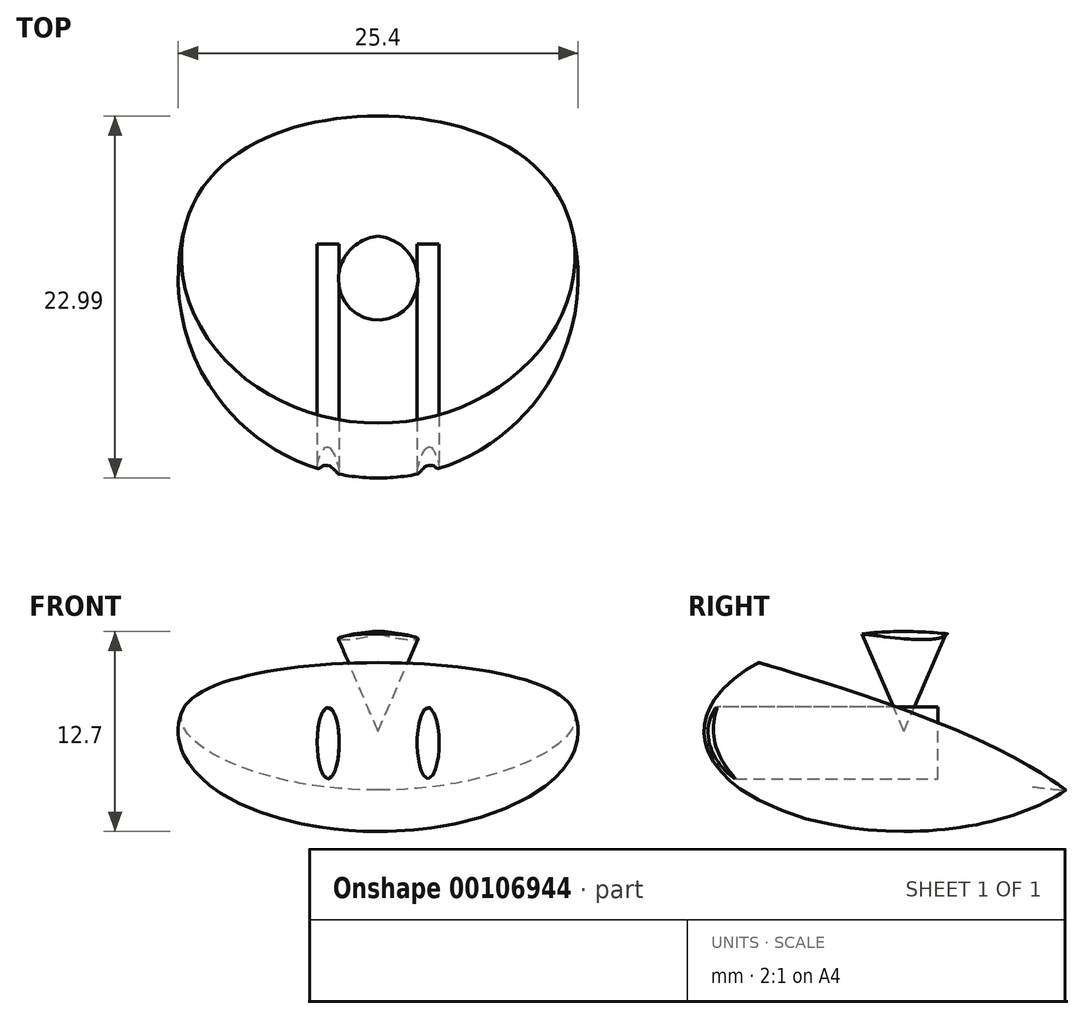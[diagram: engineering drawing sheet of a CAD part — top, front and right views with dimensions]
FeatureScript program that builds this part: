
annotation { "Feature Type Name" : "Feature", "Feature Type Description" : "" }
export const myFeature = defineFeature(function(context is Context, id is Id, definition is map)
    precondition{}
    {
        {
            var Q0;
            Q0=qCreatedBy(makeId("Right.planeOp"),FACE);
            var sketch = newSketch(context, id + "F0", { "sketchPlane" : qUnion([Q0])});
            skEllipse(sketch, "E0", {"center": v(32.9, -34.8) * mm, "majorRadius": 12.7 * mm, "minorRadius": 6.35 * mm, "majorAxis": v(1, 0)});
            skArc(sketch, "E1", {"start": v(41.65, -30.82) * mm, "mid": v(44.26, -5.42) * mm, "end": v(18.92, -2.29) * mm});
            skLineSegment(sketch, "E2", {"start": v(18.92, -2.29) * mm, "end": v(32.9, -34.8) * mm});
            skFitSpline(sketch, "E3", {"points": [v(40.84, -29.85) * mm, v(41.5, -39.46) * mm, v(-36.9, -98.21) * mm], "startDerivative": vector(25.92, -31.17) * mm, "endDerivative": vector(-0.88, 16.62) * mm, "construction": true});
            skLineSegment(sketch, "E4", {"start": v(32.9, -28.45) * mm, "end": v(32.9, -41.15) * mm});
            skLineSegment(sketch, "E5", {"start": v(32.9, -41.15) * mm, "end": v(32.9, -40.64) * mm});
            skLineSegment(sketch, "E6", {"start": v(32.9, -40.64) * mm, "end": v(36.87, -40.64) * mm, "construction": true});
            skLineSegment(sketch, "E7", {"start": v(38.84, -40.33) * mm, "end": v(40.64, -39.74) * mm, "construction": true});
            skPoint(sketch, "E8.visualSharp", {"position": v(37.88, -40.64) * mm});
            skArc(sketch, "E8.filletArc", {"start": v(36.87, -40.64) * mm, "mid": v(37.87, -40.56) * mm, "end": v(38.84, -40.33) * mm, "construction": true});
            skArc(sketch, "E9.filletArc", {"start": v(40.64, -39.74) * mm, "mid": v(41.44, -39.31) * mm, "end": v(42.03, -38.63) * mm, "construction": true});
            skFitSpline(sketch, "E10", {"points": [v(40.84, -29.85) * mm, v(42.03, -38.63) * mm, v(40.64, -39.74) * mm, v(38.84, -40.33) * mm, v(36.87, -40.64) * mm, v(32.9, -40.64) * mm], "startDerivative": vector(37.49, -37.26) * mm, "endDerivative": vector(-19.78, 0.48) * mm});
            skSolve(sketch);
        }
        {
            var Q0;
            {var subQ3=sQuery(id+"F0.wireOp",EDGE,"E0");var subQ7=makeQuery(id+"F0.imprint","INTERSECT",VERTEX,{"disambiguationData":[OD(0.0)],"derivedFrom":[subQ3,sQuery(id+"F0.wireOp",EDGE,"E3")]});Q0=makeQuery(id+"F0.imprint","IMPRINT",FACE,{"disambiguationData":[TD([[makeQuery(id+"F0.imprint","IMPRINT",EDGE,{"disambiguationData":[TD([[subQ7,1.0]])],"derivedFrom":subQ3}),-1.0]])]});}
            var Q1;
            Q1=sQuery(id+"F0.wireOp",EDGE,"E2");
            revolve(context, id + "F1", {"entities" : qUnion([Q0]), "axis" : qUnion([Q1]), "revolveType" : RevolveType.FULL});
        }
        {
            var Q0;
            {var subQ1=sQuery(id+"F0.wireOp",EDGE,"E0");var subQ4=sQuery(id+"F0.wireOp",EDGE,"E4");var subQ7=makeQuery(id+"F0.imprint","INTERSECT",VERTEX,{"derivedFrom":[subQ1,subQ4]});Q0=makeQuery(id+"F0.imprint","IMPRINT",FACE,{"disambiguationData":[TD([[makeQuery(id+"F0.imprint","IMPRINT",EDGE,{"disambiguationData":[TD([[subQ7,1.0]])],"derivedFrom":subQ1}),1.0]])]});}
            var Q1;
            Q1=sQuery(id+"F0.wireOp",EDGE,"E4");
            revolve(context, id + "F2", {"operationType" : NewBodyOperationType.ADD, "entities" : qUnion([Q0]), "axis" : qUnion([Q1]), "revolveType" : RevolveType.FULL});
        }
        {
            var Q0;
            Q0=qCreatedBy(makeId("Front.planeOp"),FACE);
            var sketch = newSketch(context, id + "F3", { "sketchPlane" : qUnion([Q0])});
            skCircle(sketch, "E11", {"center": v(0, -12.26) * mm, "radius": 11.27 * mm});
            skLineSegment(sketch, "E12", {"start": v(0, -30.43) * mm, "end": v(0, -40.63) * mm, "construction": true});
            skLineSegment(sketch, "E13", {"start": v(0, -35.53) * mm, "end": v(2.48, -35.53) * mm, "construction": true});
            skEllipse(sketch, "E14", {"center": v(3.18, -35.53) * mm, "majorRadius": 2.27 * mm, "minorRadius": 0.7 * mm, "majorAxis": v(0, -1)});
            skEllipse(sketch, "E15.MirrorC", {"center": v(-3.18, -35.53) * mm, "majorRadius": 2.27 * mm, "minorRadius": 0.7 * mm, "majorAxis": v(0, -1)});
            skLineSegment(sketch, "E16.MirrorCS", {"start": v(0, -35.53) * mm, "end": v(-2.48, -35.53) * mm, "construction": true});
            skLineSegment(sketch, "E17", {"start": v(11.27, -12.26) * mm, "end": v(29.27, -12.26) * mm, "construction": true});
            skLineSegment(sketch, "E18", {"start": v(-11.27, -12.26) * mm, "end": v(-29.66, -12.26) * mm, "construction": true});
            skLineSegment(sketch, "E19", {"start": v(-29.66, -12.26) * mm, "end": v(29.27, -12.26) * mm, "construction": true});
            skLineSegment(sketch, "E20", {"start": v(-2.48, -35.53) * mm, "end": v(-3.18, -35.53) * mm, "construction": true});
            skLineSegment(sketch, "E21", {"start": v(2.48, -35.53) * mm, "end": v(3.18, -35.53) * mm, "construction": true});
            skLineSegment(sketch, "E22", {"start": v(0, 0) * mm, "end": v(0, -30.43) * mm, "construction": true});
            skSolve(sketch);
        }
        {
            var Q0;
            Q0=qCreatedBy(makeId("Right.planeOp"),FACE);
            var sketch = newSketch(context, id + "F4", { "sketchPlane" : qUnion([Q0])});
            skLineSegment(sketch, "E23", {"start": v(0, 0) * mm, "end": v(56.12, 0) * mm, "construction": true});
            skLineSegment(sketch, "E24", {"start": v(56.12, 0) * mm, "end": v(56.12, -42.87) * mm, "construction": true});
            skLineSegment(sketch, "E25", {"start": v(0, -42.87) * mm, "end": v(0, -40.58) * mm, "construction": true});
            skLineSegment(sketch, "E26", {"start": v(0, -40.58) * mm, "end": v(56.12, -40.58) * mm, "construction": true});
            skLineSegment(sketch, "E27", {"start": v(0, 0) * mm, "end": v(0, -40.58) * mm, "construction": true});
            skLineSegment(sketch, "E28", {"start": v(0, -42.87) * mm, "end": v(56.12, -42.87) * mm});
            skLineSegment(sketch, "E29", {"start": v(28.06, -42.87) * mm, "end": v(28.06, 0) * mm, "construction": true});
            skSolve(sketch);
        }
        {
            var Q0;
            Q0=makeQuery(id+"F1.opRevolve","SWEPT_BODY",BODY,{"disambiguationData":[OSD([sQuery(id+"F0.wireOp",EDGE,"E0"),sQuery(id+"F0.wireOp",EDGE,"E1"),sQuery(id+"F0.wireOp",EDGE,"E2")])]});
            var Q1;
            Q1=sQuery(id+"F4.wireOp",EDGE,"E29");
            transform(context, id + "F5", {"entities" : qUnion([Q0]), "transformType" : TransformType.ROTATION, "transformAxis" : qUnion([Q1]), "angle" : 180 * degree, "makeCopy" : false});
        }
        {
            var Q0;
            Q0=qCreatedBy(makeId("Right.planeOp"),FACE);
            var sketch = newSketch(context, id + "F6", { "sketchPlane" : qUnion([Q0])});
            skCircle(sketch, "E30", {"center": v(31.4, -16.66) * mm, "radius": 11.26 * mm});
            skSolve(sketch);
        }
        {
            var Q0;
            Q0 = qSketchRegion(id + "F6", true);
            var Q1;
            Q1=sQuery(id+"F6.wireOp",EDGE,"E30");
            var Q2;
            Q2=makeQuery(id+"F1.opRevolve","SWEPT_BODY",BODY,{"disambiguationData":[OSD([sQuery(id+"F0.wireOp",EDGE,"E0"),sQuery(id+"F0.wireOp",EDGE,"E1"),sQuery(id+"F0.wireOp",EDGE,"E2")])]});
            var Q3;
            Q3=makeQuery(id+"F1.opRevolve","SWEPT_BODY",BODY,{"disambiguationData":[OSD([sQuery(id+"F0.wireOp",EDGE,"E0"),sQuery(id+"F0.wireOp",EDGE,"E1"),sQuery(id+"F0.wireOp",EDGE,"E2")])]});
            extrude(context, id + "F7", {"entities" : qUnion([Q0]), "bodyType" : ToolBodyType.SURFACE, "operationType" : NewBodyOperationType.INTERSECT, "surfaceEntities" : qUnion([Q1]), "endBound" : BoundingType.UP_TO_BODY, "endBoundEntityBody" : qUnion([Q2]), "depth" : 22.86 * mm, "hasSecondDirection" : true, "secondDirectionBound" : SecondDirectionBoundingType.UP_TO_BODY, "secondDirectionOppositeDirection" : true, "secondDirectionBoundEntityBody" : qUnion([Q3]), "secondDirectionDepth" : 25.4 * mm});
        }
        {
            var Q0;
            Q0=makeQuery(id+"F1.opRevolve","SWEPT_BODY",BODY,{"disambiguationData":[OSD([sQuery(id+"F0.wireOp",EDGE,"E0"),sQuery(id+"F0.wireOp",EDGE,"E1"),sQuery(id+"F0.wireOp",EDGE,"E2")])]});
            var Q1;
            Q1=makeQuery(id+"F7.opExtrude","SWEPT_BODY",BODY,{"disambiguationData":[OSD([sQuery(id+"F6.wireOp",EDGE,"E30")])]});
            var Q2;
            Q2=sQuery(id+"F4.wireOp",EDGE,"E28");
            var Q3;
            Q3=sQuery(id+"F4.wireOp",EDGE,"E28");
            transform(context, id + "F8", {"entities" : qUnion([Q0, Q1]), "transformType" : TransformType.TRANSLATION_DISTANCE, "transformDirection" : qUnion([Q3]), "distance" : 25.4 * mm, "oppositeDirection" : true, "makeCopy" : false});
        }
        {
            var Q0;
            Q0 = qSketchRegion(id + "F3", true);
            var Q1;
            Q1=sQuery(id+"F3.wireOp",EDGE,"E11");
            var Q2;
            Q2=sQuery(id+"F3.wireOp",EDGE,"E14");
            var Q3;
            Q3=sQuery(id+"F3.wireOp",EDGE,"E15.MirrorC");
            var Q4;
            Q4=makeQuery(id+"F1.opRevolve","SWEPT_BODY",BODY,{"disambiguationData":[OSD([sQuery(id+"F0.wireOp",EDGE,"E0"),sQuery(id+"F0.wireOp",EDGE,"E1"),sQuery(id+"F0.wireOp",EDGE,"E2")])]});
            extrude(context, id + "F9", {"entities" : qUnion([Q0]), "operationType" : NewBodyOperationType.REMOVE, "surfaceEntities" : qUnion([Q1, Q2, Q3]), "endBound" : BoundingType.UP_TO_BODY, "endBoundEntityBody" : qUnion([Q4]), "depth" : 25.4 * mm});
        }
    });
